# Revit family: MicroMix (a)
name_source: partatom
category: Equipement spécialisé
revit_build: Autodesk Revit LT 2015 (Build: 20140606_1530(x64)
units: mm (PartAtom-declared; Revit-internal decimal feet)

## types (4) — shared parameters
Apparent Power = 0 VA
Depth = 68 mm
Depth Electrique connexion = 34 mm
Description = MIXERS PLONGEANTS
Fabricant = ROBOT COUPE
Height = 420 mm  [stored 1.37795 ft]
Height Electrique connexion = 410 mm  [stored 1.34514 ft]
Modèle = MicroMix
Phase = 1
Speeds (Rpm) = 1500 to 14000
URL = www.robot-coupe.com
Watts = 220 W
Weight = 1.4 kg
Width = 110 mm  [stored 0.360892 ft]
water = Connector
zero-valued in all types: Cold water supply, Cold water supply height, Used water, Waste water height

## per-type parameters (varying)
| type | Cycle | Volts |
| MicroMix   120/60/1 | 60 Hz | 120 V |
| MicroMix   230/50/1 | 50 Hz | 230 V |
| MicroMix   220/60/1 | 60 Hz | 220 V |
| MicroMix   240/50/1 | 50 Hz | 240 V |

note: [stored X ft] marks values corroborated as IEEE doubles in the binary element streams (Revit-internal decimal feet)

## geometry (parser evidence)
native form markers: Blend x106, Sweep x4
no freeform markers — native parametric forms only
